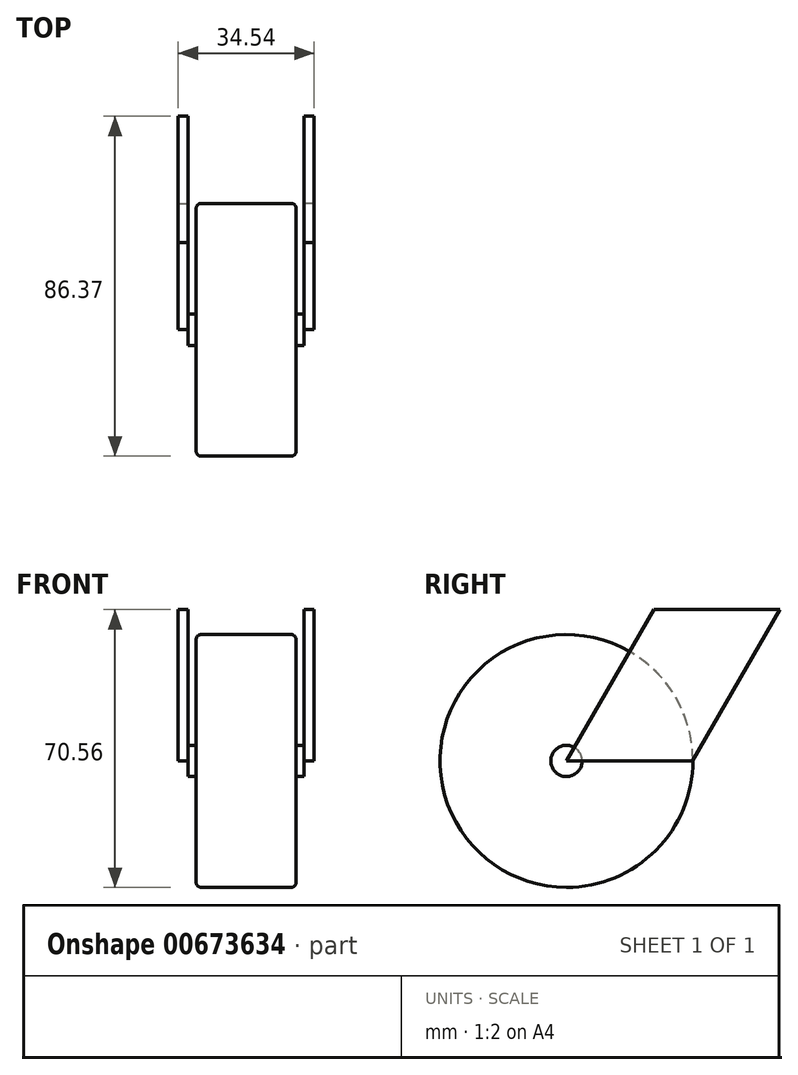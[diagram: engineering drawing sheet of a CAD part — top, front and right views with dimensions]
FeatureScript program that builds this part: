
annotation { "Feature Type Name" : "Feature", "Feature Type Description" : "" }
export const myFeature = defineFeature(function(context is Context, id is Id, definition is map)
    precondition{}
    {
        {
            var Q0;
            Q0=qCreatedBy(makeId("Right.planeOp"),FACE);
            var sketch = newSketch(context, id + "F0", { "sketchPlane" : qUnion([Q0])});
            skCircle(sketch, "E0", {"center": v(0, 0) * mm, "radius": 32.11 * mm});
            skSolve(sketch);
        }
        {
            var Q0;
            Q0=makeQuery(id+"F0.imprint","IMPRINT",FACE,{"disambiguationData":[TD([[makeQuery(id+"F0.imprint","IMPRINT",EDGE,{"derivedFrom":sQuery(id+"F0.wireOp",EDGE,"E0")}),1.0]])]});
            extrude(context, id + "F1", {"entities" : qUnion([Q0]), "depth" : 25.4 * mm, "offsetDistance" : 25.4 * mm});
        }
        {
            var Q0;
            Q0=makeQuery(id+"F1.opExtrude","CAP_EDGE",EDGE,{"disambiguationData":[OSD([sQuery(id+"F0.wireOp",EDGE,"E0")])],"isStart":false});
            fillet(context, id + "F2", {"entities" : qUnion([Q0]), "radius" : 1.27 * mm, "tangentPropagation" : true, "allowEdgeOverflow" : false});
        }
        {
            var Q0;
            Q0=makeQuery(id+"F1.opExtrude","CAP_EDGE",EDGE,{"disambiguationData":[OSD([sQuery(id+"F0.wireOp",EDGE,"E0")])],"isStart":true});
            fillet(context, id + "F3", {"entities" : qUnion([Q0]), "radius" : 1.27 * mm, "tangentPropagation" : true, "allowEdgeOverflow" : false});
        }
        {
            var Q0;
            Q0=makeQuery(id+"F1.opExtrude","CAP_FACE",FACE,{"disambiguationData":[OSD([sQuery(id+"F0.wireOp",EDGE,"E0")])],"isStart":false});
            var sketch = newSketch(context, id + "F4", { "sketchPlane" : qUnion([Q0])});
            skCircle(sketch, "E1", {"center": v(0, 0) * mm, "radius": 3.98 * mm});
            skSolve(sketch);
        }
        {
            var Q0;
            Q0=qSketchRegion(id+"F4",true);
            extrude(context, id + "F5", {"entities" : qUnion([Q0]), "operationType" : NewBodyOperationType.ADD, "depth" : 2.03 * mm, "offsetDistance" : 25.4 * mm});
        }
        {
            var Q0;
            Q0=makeQuery(id+"F1.opExtrude","CAP_FACE",FACE,{"disambiguationData":[OSD([sQuery(id+"F0.wireOp",EDGE,"E0")])],"isStart":true});
            var sketch = newSketch(context, id + "F6", { "sketchPlane" : qUnion([Q0])});
            skSolve(sketch);
        }
        {
            var Q0;
            {var subQ0=sQuery(id+"F0.wireOp",EDGE,"E0");Q0=makeQuery(id+"F6.imprint","IMPRINT",FACE,{"disambiguationData":[TD([[makeQuery(id+"F6.imprint","IMPRINT",EDGE,{"derivedFrom":makeQuery(id+"F3.opFillet","BLEND_EDGE",EDGE,{"blendedFrom":[makeQuery(id+"F1.opExtrude","CAP_EDGE",EDGE,{"disambiguationData":[OSD([subQ0])],"isStart":true}),makeQuery(id+"F1.opExtrude","CAP_FACE",FACE,{"disambiguationData":[OSD([subQ0])],"isStart":true})],"blendedInto":[makeQuery(id+"F1.opExtrude","CAP_FACE",FACE,{"disambiguationData":[OSD([subQ0])],"isStart":true})]})}),1.0]])]});}
            var sketch = newSketch(context, id + "F7", { "sketchPlane" : qUnion([Q0])});
            skCircle(sketch, "E2", {"center": v(0, 0) * mm, "radius": 3.98 * mm});
            skSolve(sketch);
        }
        {
            var Q0;
            Q0=qSketchRegion(id+"F7",true);
            extrude(context, id + "F8", {"entities" : qUnion([Q0]), "operationType" : NewBodyOperationType.ADD, "depth" : 2.03 * mm, "offsetDistance" : 25.4 * mm});
        }
        {
            var Q0;
            Q0=makeQuery(id+"F8.opExtrude","CAP_FACE",FACE,{"disambiguationData":[OSD([sQuery(id+"F7.wireOp",EDGE,"E2")])],"isStart":false});
            var sketch = newSketch(context, id + "F9", { "sketchPlane" : qUnion([Q0])});
            skLineSegment(sketch, "E3", {"start": v(0, 0) * mm, "end": v(-22.2, 38.45) * mm});
            skLineSegment(sketch, "E4", {"start": v(-22.2, 38.45) * mm, "end": v(-54.26, 38.45) * mm});
            skLineSegment(sketch, "E5", {"start": v(-54.26, 38.45) * mm, "end": v(-32.06, 0) * mm});
            skLineSegment(sketch, "E6", {"start": v(-32.06, 0) * mm, "end": v(0, 0) * mm});
            skSolve(sketch);
        }
        {
            var Q0;
            {var subQ4=sQuery(id+"F9.wireOp",EDGE,"E4");Q0=makeQuery(id+"F9.imprint","IMPRINT",FACE,{"disambiguationData":[TD([[makeQuery(id+"F9.imprint","IMPRINT",EDGE,{"derivedFrom":subQ4}),1.0]])]});}
            var Q1;
            {var subQ0=sQuery(id+"F9.wireOp",EDGE,"E6");var subQ1=sQuery(id+"F9.wireOp",EDGE,"E3");var subQ2=makeQuery(id+"F9.imprint","INTERSECT",VERTEX,{"derivedFrom":[subQ1,subQ0]});Q1=makeQuery(id+"F9.imprint","IMPRINT",FACE,{"disambiguationData":[TD([[makeQuery(id+"F9.imprint","IMPRINT",EDGE,{"disambiguationData":[TD([[subQ2,-1.0]])],"derivedFrom":subQ1}),1.0]])]});}
            extrude(context, id + "F10", {"entities" : qUnion([Q0, Q1]), "operationType" : NewBodyOperationType.ADD, "depth" : 2.54 * mm, "offsetDistance" : 25.4 * mm});
        }
        {
            var Q0;
            Q0=makeQuery(id+"F5.opExtrude","CAP_FACE",FACE,{"disambiguationData":[OSD([sQuery(id+"F4.wireOp",EDGE,"E1")])],"isStart":false});
            var sketch = newSketch(context, id + "F11", { "sketchPlane" : qUnion([Q0])});
            skLineSegment(sketch, "E7.0", {"start": v(54.26, 38.45) * mm, "end": v(32.06, 0) * mm});
            skLineSegment(sketch, "E7.1", {"start": v(22.2, 38.45) * mm, "end": v(54.26, 38.45) * mm});
            skLineSegment(sketch, "E7.2", {"start": v(0, 0) * mm, "end": v(22.2, 38.45) * mm});
            skLineSegment(sketch, "E7.3", {"start": v(32.06, 0) * mm, "end": v(0, 0) * mm});
            skSolve(sketch);
        }
        {
            var Q0;
            Q0=qSketchRegion(id+"F11",true);
            extrude(context, id + "F12", {"entities" : qUnion([Q0]), "operationType" : NewBodyOperationType.ADD, "depth" : 2.54 * mm, "offsetDistance" : 25.4 * mm});
        }
    });
